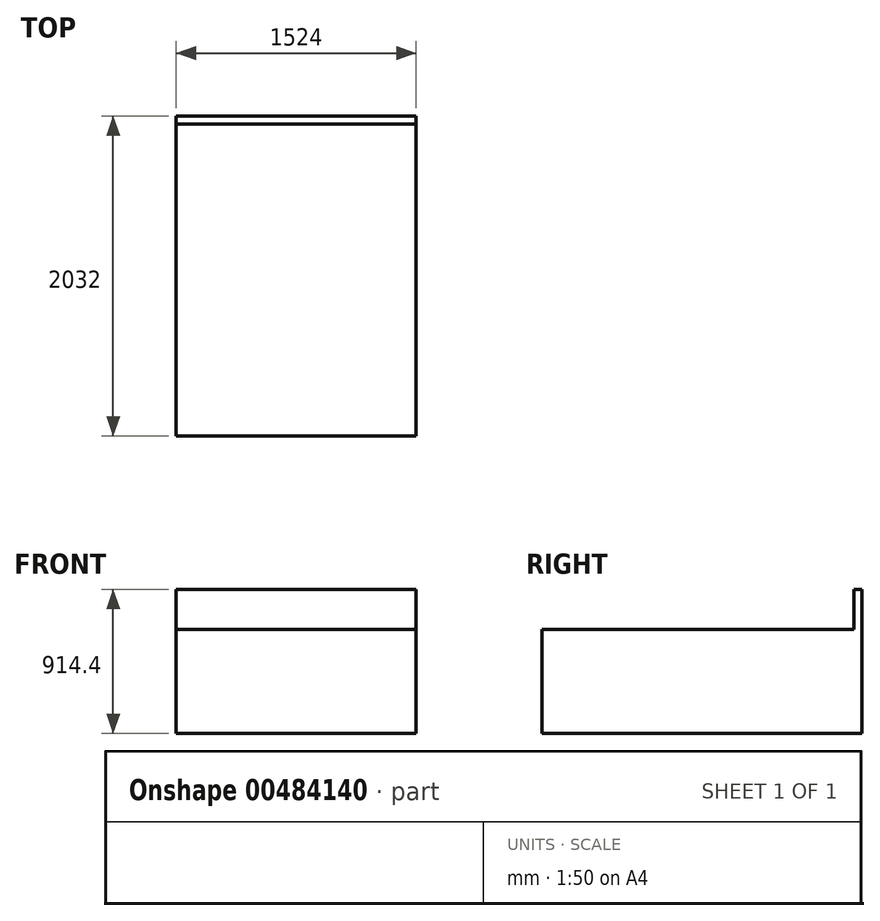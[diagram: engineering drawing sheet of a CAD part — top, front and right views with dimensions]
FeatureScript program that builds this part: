
annotation { "Feature Type Name" : "Feature", "Feature Type Description" : "" }
export const myFeature = defineFeature(function(context is Context, id is Id, definition is map)
    precondition{}
    {
        {
            var Q0;
            Q0=qCreatedBy(makeId("Top.planeOp"),FACE);
            var sketch = newSketch(context, id + "F0", { "sketchPlane" : qUnion([Q0])});
            skLineSegment(sketch, "E0.bottom", {"start": v(0, 0) * mm, "end": v(1524, 0) * mm});
            skLineSegment(sketch, "E0.top", {"start": v(0, 1981.2) * mm, "end": v(1524, 1981.2) * mm});
            skLineSegment(sketch, "E0.left", {"start": v(0, 0) * mm, "end": v(0, 1981.2) * mm});
            skLineSegment(sketch, "E0.right", {"start": v(1524, 0) * mm, "end": v(1524, 1981.2) * mm});
            skSolve(sketch);
        }
        {
            var Q0;
            Q0 = qSketchRegion(id + "F0", true);
            extrude(context, id + "F1", {"entities" : qUnion([Q0]), "depth" : 660.4 * mm, "offsetDistance" : 25.4 * mm});
        }
        {
            var Q0;
            Q0=qCreatedBy(makeId("Right.planeOp"),FACE);
            var sketch = newSketch(context, id + "F2", { "sketchPlane" : qUnion([Q0])});
            skLineSegment(sketch, "E1.bottom", {"start": v(1981.2, 0) * mm, "end": v(2032, 0) * mm});
            skLineSegment(sketch, "E1.top", {"start": v(1981.2, 914.4) * mm, "end": v(2032, 914.4) * mm});
            skLineSegment(sketch, "E1.left", {"start": v(1981.2, 0) * mm, "end": v(1981.2, 914.4) * mm});
            skLineSegment(sketch, "E1.right", {"start": v(2032, 0) * mm, "end": v(2032, 914.4) * mm});
            skSolve(sketch);
        }
        {
            var Q0;
            Q0 = qSketchRegion(id + "F2", true);
            var Q1;
            Q1=makeQuery(id+"F1.opExtrude","SWEPT_FACE",FACE,{"disambiguationData":[OSD([sQuery(id+"F0.wireOp",EDGE,"E0.right")])]});
            extrude(context, id + "F3", {"entities" : qUnion([Q0]), "operationType" : NewBodyOperationType.ADD, "endBound" : BoundingType.UP_TO_SURFACE, "depth" : 25.4 * mm, "endBoundEntityFace" : qUnion([Q1]), "offsetDistance" : 25.4 * mm});
        }
    });
